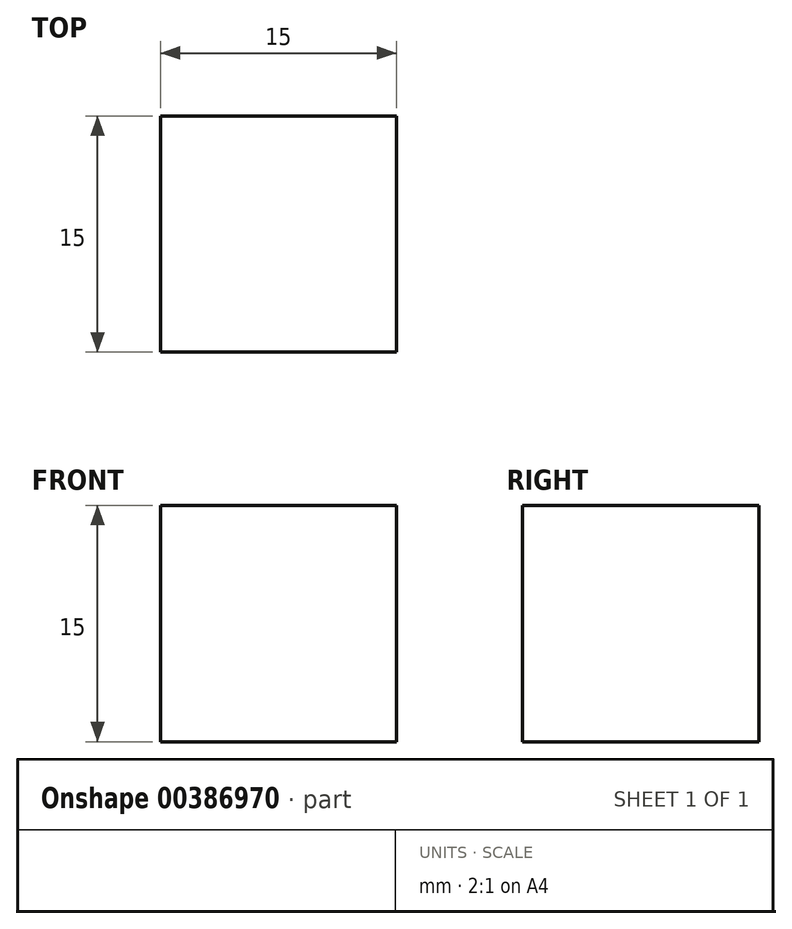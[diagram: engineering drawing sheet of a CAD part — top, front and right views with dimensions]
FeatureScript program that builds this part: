
annotation { "Feature Type Name" : "Feature", "Feature Type Description" : "" }
export const myFeature = defineFeature(function(context is Context, id is Id, definition is map)
    precondition{}
    {
        {
            var Q0;
            Q0=qCreatedBy(makeId("Top.planeOp"),FACE);
            var sketch = newSketch(context, id + "F0", { "sketchPlane" : qUnion([Q0])});
            skLineSegment(sketch, "E0.bottom", {"start": v(0, 0) * mm, "end": v(15, 0) * mm});
            skLineSegment(sketch, "E0.top", {"start": v(0, 15) * mm, "end": v(15, 15) * mm});
            skLineSegment(sketch, "E0.left", {"start": v(0, 0) * mm, "end": v(0, 15) * mm});
            skLineSegment(sketch, "E0.right", {"start": v(15, 0) * mm, "end": v(15, 15) * mm});
            skSolve(sketch);
        }
        {
            var Q0;
            Q0 = qSketchRegion(id + "F0", true);
            extrude(context, id + "F1", {"entities" : qUnion([Q0]), "depth" : 15 * mm});
        }
    });
